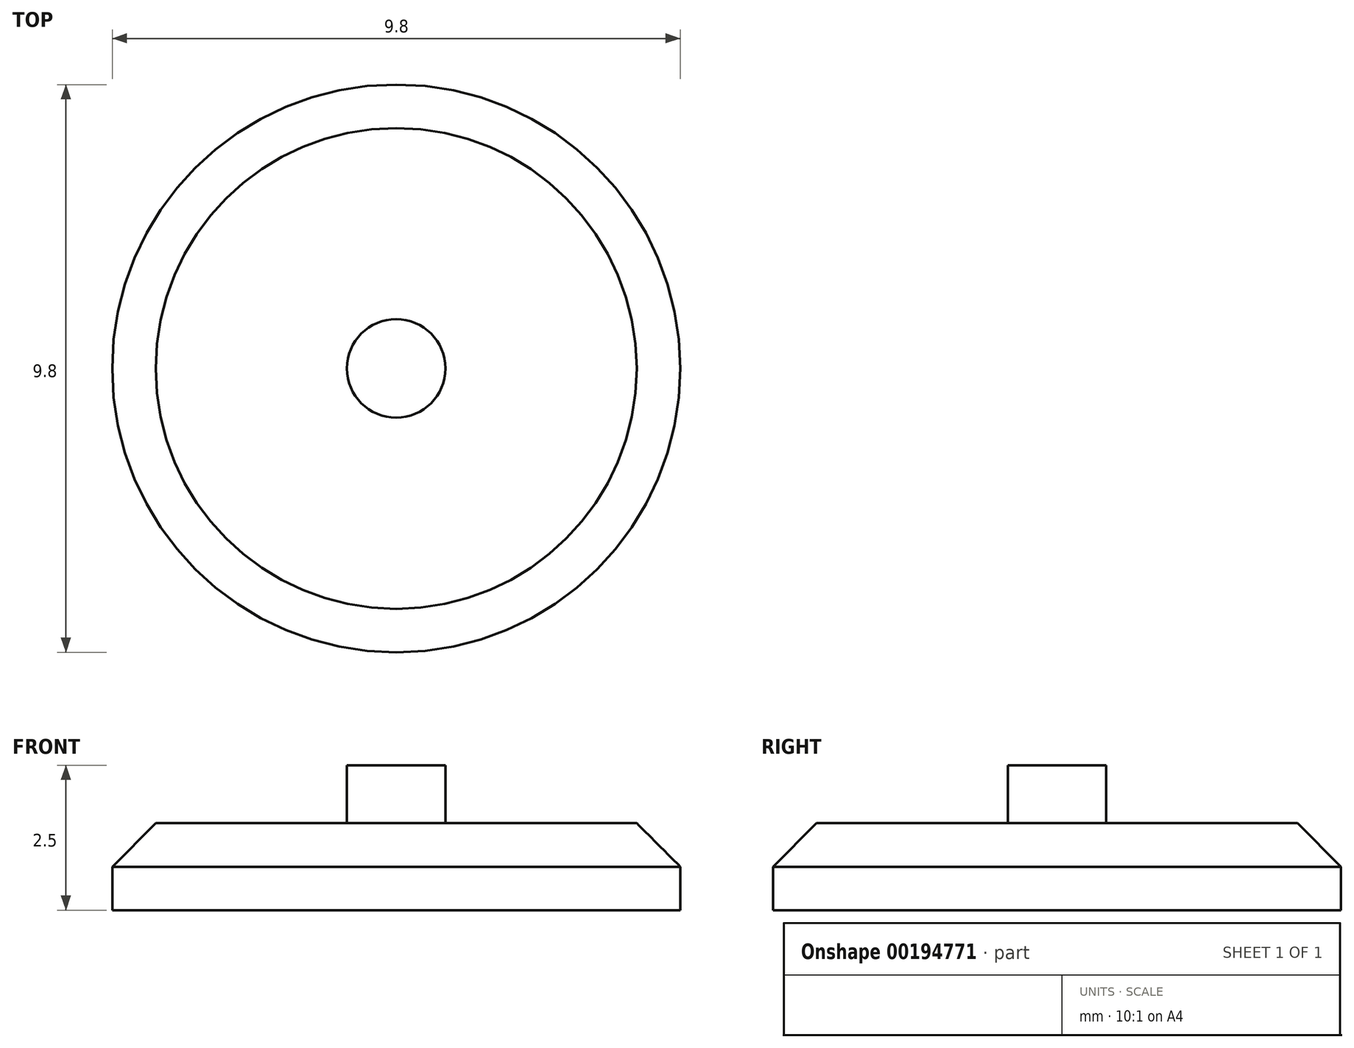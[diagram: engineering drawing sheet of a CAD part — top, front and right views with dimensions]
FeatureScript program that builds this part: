
annotation { "Feature Type Name" : "Feature", "Feature Type Description" : "" }
export const myFeature = defineFeature(function(context is Context, id is Id, definition is map)
    precondition{}
    {
        {
            var Q0;
            Q0=qCreatedBy(makeId("Top.planeOp"),FACE);
            var sketch = newSketch(context, id + "F0", { "sketchPlane" : qUnion([Q0])});
            skCircle(sketch, "E0", {"center": v(0, 0) * mm, "radius": 0.85 * mm});
            skCircle(sketch, "E1.0", {"center": v(0, 0) * mm, "radius": 4.9 * mm});
            skSolve(sketch);
        }
        {
            var Q0;
            Q0=makeQuery(id+"F0.imprint","IMPRINT",FACE,{"disambiguationData":[TD([[makeQuery(id+"F0.imprint","IMPRINT",EDGE,{"derivedFrom":sQuery(id+"F0.wireOp",EDGE,"E0")}),1.0]])]});
            extrude(context, id + "F1", {"entities" : qUnion([Q0]), "depth" : 1 * mm});
        }
        {
            var Q0;
            Q0=makeQuery(id+"F0.imprint","IMPRINT",FACE,{"disambiguationData":[TD([[makeQuery(id+"F0.imprint","IMPRINT",EDGE,{"derivedFrom":sQuery(id+"F0.wireOp",EDGE,"E0")}),-1.0]])]});
            var Q1;
            Q1=makeQuery(id+"F0.imprint","IMPRINT",FACE,{"disambiguationData":[TD([[makeQuery(id+"F0.imprint","IMPRINT",EDGE,{"derivedFrom":sQuery(id+"F0.wireOp",EDGE,"E0")}),1.0]])]});
            extrude(context, id + "F2", {"entities" : qUnion([Q0, Q1]), "operationType" : NewBodyOperationType.ADD, "oppositeDirection" : true, "depth" : 1.5 * mm});
        }
        {
            var Q0;
            Q0=makeQuery(id+"F2.opExtrude","CAP_EDGE",EDGE,{"disambiguationData":[OSD([sQuery(id+"F0.wireOp",EDGE,"E1.0")])],"isStart":true});
            chamfer(context, id + "F3", {"entities" : qUnion([Q0]), "width" : 0.75 * mm, "tangentPropagation" : true});
        }
    });
